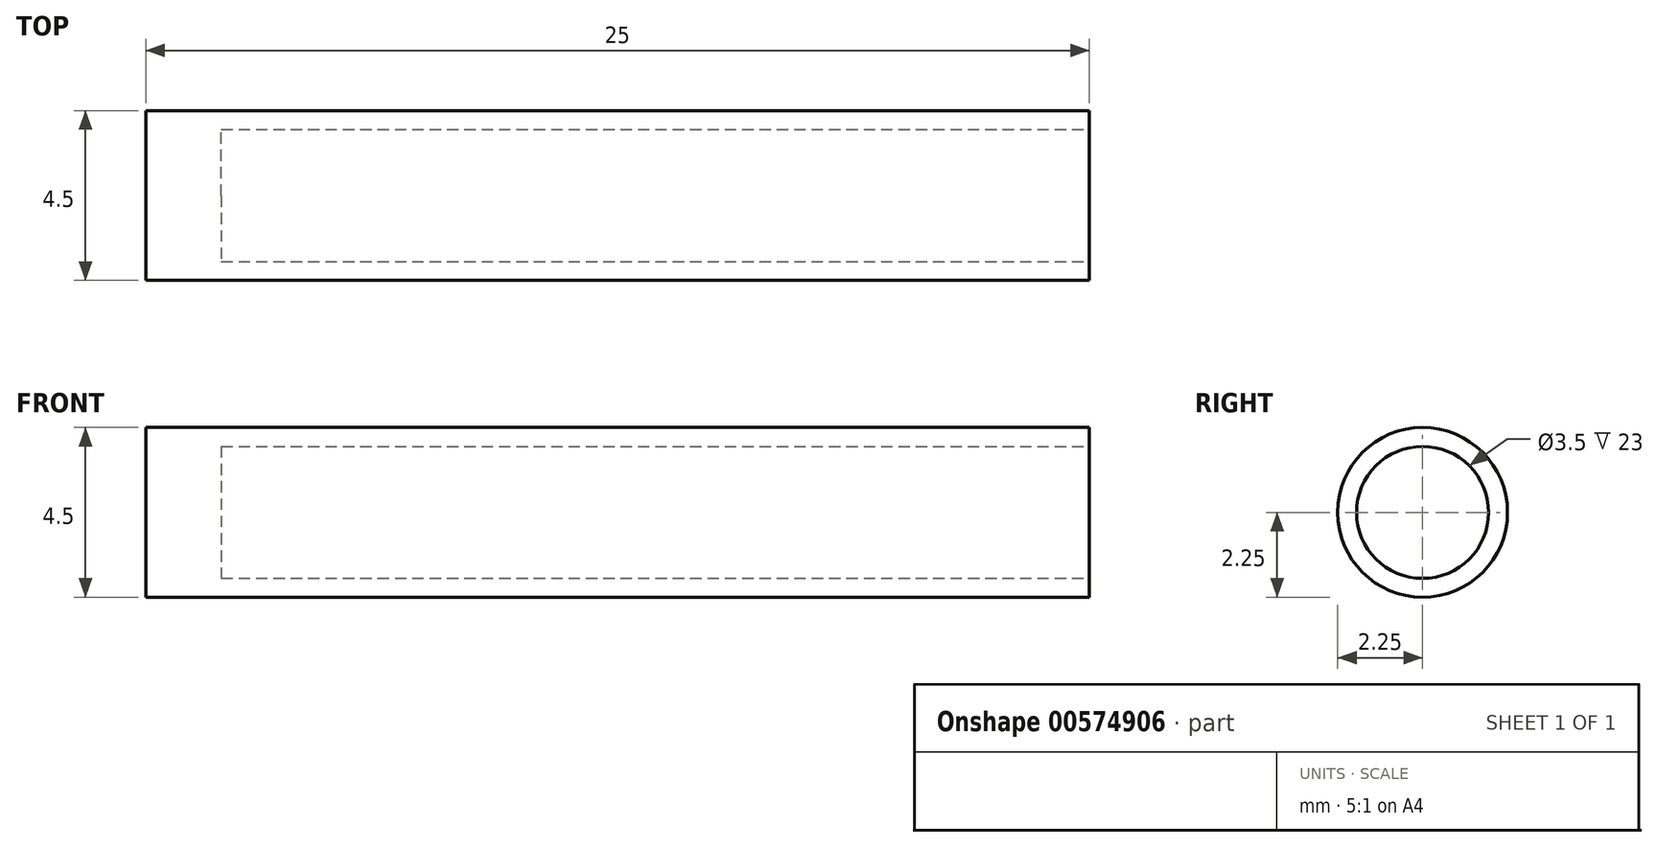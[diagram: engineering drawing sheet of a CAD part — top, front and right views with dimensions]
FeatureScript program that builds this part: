
annotation { "Feature Type Name" : "Feature", "Feature Type Description" : "" }
export const myFeature = defineFeature(function(context is Context, id is Id, definition is map)
    precondition{}
    {
        {
            var Q0;
            Q0=qCreatedBy(makeId("Right.planeOp"),FACE);
            var sketch = newSketch(context, id + "F0", { "sketchPlane" : qUnion([Q0])});
            skCircle(sketch, "E0", {"center": v(0, 0) * mm, "radius": 2.25 * mm});
            skCircle(sketch, "E1.0", {"center": v(0, 0) * mm, "radius": 1.75 * mm});
            skSolve(sketch);
        }
        {
            var Q0;
            Q0 = qSketchRegion(id + "F0", true);
            extrude(context, id + "F1", {"entities" : qUnion([Q0]), "oppositeDirection" : true, "depth" : 25 * mm, "offsetDistance" : 25 * mm});
        }
        {
            var Q0;
            Q0=makeQuery(id+"F1.opExtrude","CAP_FACE",FACE,{"disambiguationData":[OSD([sQuery(id+"F0.wireOp",EDGE,"E0"),sQuery(id+"F0.wireOp",EDGE,"E1.0")])],"isStart":false});
            var sketch = newSketch(context, id + "F2", { "sketchPlane" : qUnion([Q0])});
            skCircle(sketch, "E2.0", {"center": v(0, 0) * mm, "radius": 1.75 * mm});
            skSolve(sketch);
        }
        {
            var Q0;
            Q0 = qSketchRegion(id + "F2", true);
            extrude(context, id + "F3", {"entities" : qUnion([Q0]), "operationType" : NewBodyOperationType.ADD, "oppositeDirection" : true, "depth" : 2 * mm, "offsetDistance" : 25 * mm});
        }
    });
